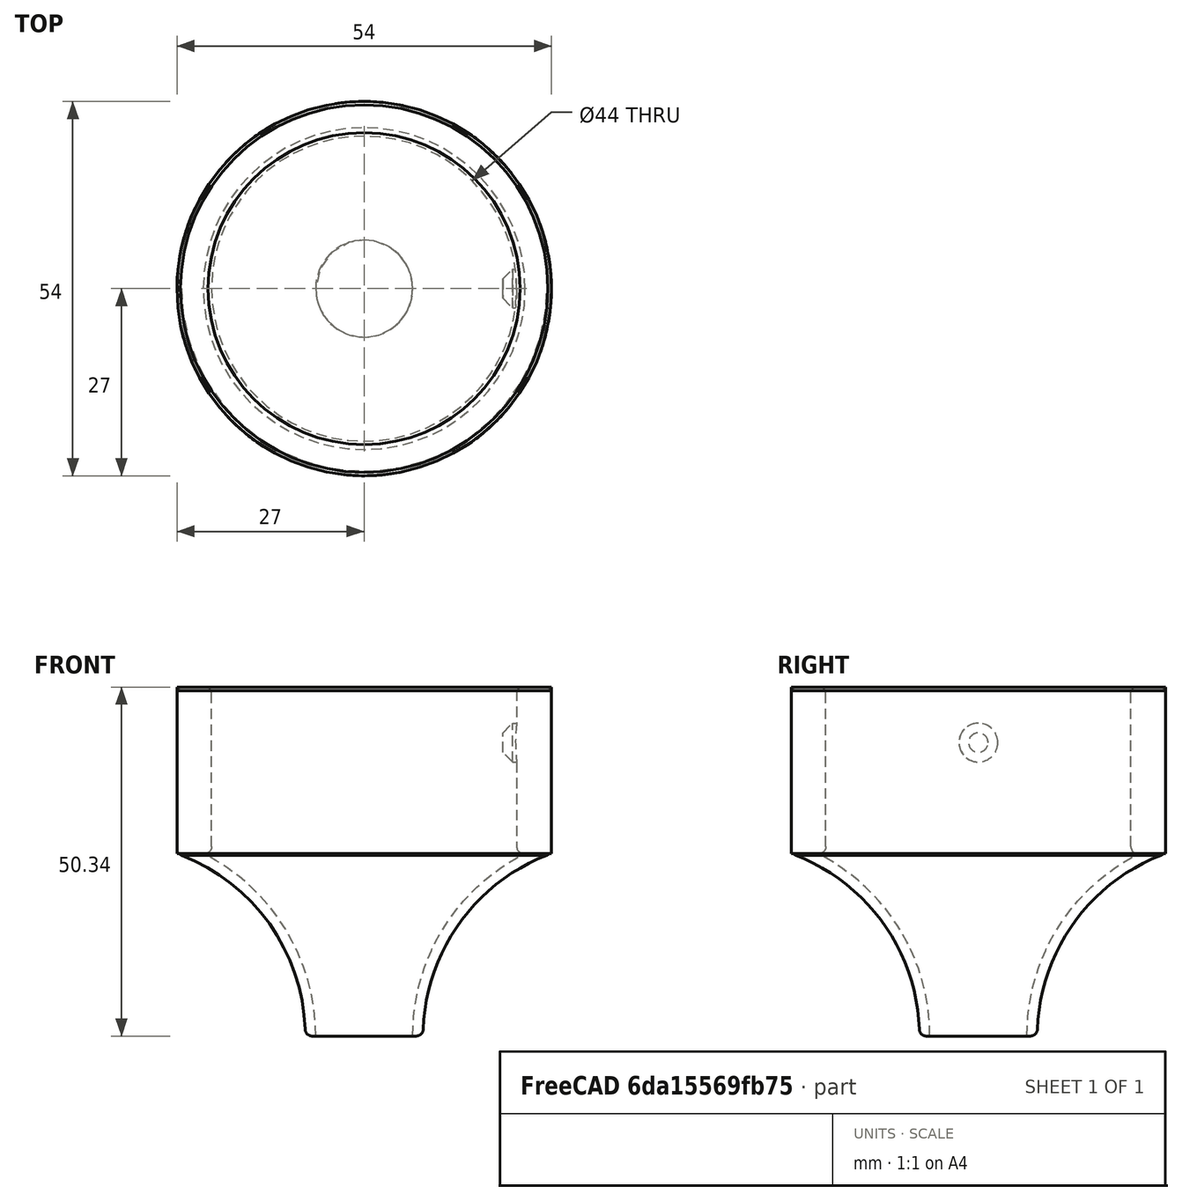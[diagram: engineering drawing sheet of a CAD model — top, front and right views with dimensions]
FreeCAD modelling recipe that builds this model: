
FCSTD DOCUMENT  (FreeCAD 0.16R)
Label: BlowerNozzle
License: All rights reserved
LicenseURL: http://en.wikipedia.org/wiki/All_rights_reserved
objects: Sketcher::SketchObject×3, Part::Fillet×2, Part::Chamfer×2, PartDesign::Pad×1, PartDesign::Pocket×1, PartDesign::Revolution×1, Part::Cylinder×1, Part::MultiFuse×1, Mesh::Feature×1
note: 15 computed .brp shape members not serialized (recipe doc carries the construction recipe); baked Part::Feature solids carry a one-line shape summary decoded from their .brp

FEATURE [Sketcher::SketchObject] Sketch
  sketch-geometry (1):
    g0: Circle CenterX=0 CenterY=0 CenterZ=0 NormalX=0 NormalY=0 NormalZ=1 Radius=27
  constraints (2):
    c: Radius(g0) = 27
    c: Coincident(g0,g-1)
FEATURE [PartDesign::Pad] Pad
  Length = 24
  Length2 = 100
  Sketch = -> Sketch
  Type = 0
FEATURE [Sketcher::SketchObject] Sketch001
  Placement = pos=(0,0,24) rot=(0,0,1;0rad)
  Support = -> Pad [Face3]
  sketch-geometry (1):
    g0: Circle CenterX=0 CenterY=0 CenterZ=0 NormalX=0 NormalY=0 NormalZ=1 Radius=22
  constraints (2):
    c: Coincident(g0,g-1)
    c: Radius(g0) = 22
FEATURE [PartDesign::Pocket] Pocket
  Length = 5
  Sketch = -> Sketch001
  Type = 1
FEATURE [Sketcher::SketchObject] Sketch002
  Placement = pos=(0,0,0) rot=(-1,0,0;4.71239rad)
  sketch-geometry (5):
    g0: ArcOfCircle CenterX=-36.5 CenterY=-26.3391 CenterZ=0 NormalX=0 NormalY=0 NormalZ=1 Radius=28 StartAngle=6.28318 EndAngle=7.50782
    g1: ArcOfCircle CenterX=-36.5 CenterY=-26.3391 CenterZ=0 NormalX=0 NormalY=0 NormalZ=1 Radius=29.5 StartAngle=6.28318 EndAngle=7.38682
    g2: LineSegment [constr] StartX=-7 StartY=-13.456 StartZ=0 EndX=-7 EndY=-26.3392 EndZ=0
    g3: LineSegment StartX=-8.5 StartY=-26.3392 StartZ=0 EndX=-7 EndY=-26.3392 EndZ=0
    g4: LineSegment StartX=-27 StartY=0 StartZ=0 EndX=-23.2147 EndY=0 EndZ=0
  constraints (16):
    c: Radius(g0) = 28
    c: Coincident(g1,g0)
    c: Radius(g1) = 29.5
    c: Vertical(g2)
    c: DistanceX(g2) = -7
    c: Coincident(g1,g2)
    c: Tangent(g1,g2)
    c: PointOnObject(g1,g-1)
    c: DistanceX(g0) = -27
    c: PointOnObject(g0,g-1)
    c: Coincident(g3,g0)
    c: Coincident(g3,g1)
    c: Horizontal(g3)
    c: Coincident(g4,g0)
    c: Coincident(g4,g1)
    c: Distance(g2) = 12.8832
FEATURE [PartDesign::Revolution] Revolution
  Angle = 360
  Axis = (0,0,1)
  Base = (0,0,0)
  Placement = pos=(0,0,0) rot=(-1,0,0;4.71239rad)
  ReferenceAxis = -> Sketch002 [V_Axis]
  Sketch = -> Sketch002
FEATURE [Part::Cylinder] Cylinder
  Angle = 360
  Height = 5
  Placement = pos=(20,0,16) rot=(0,1,0;1.5708rad)
  Radius = 2.8
FEATURE [Part::MultiFuse] Fusion
  Shapes = -> [Pocket,Revolution,Cylinder]
FEATURE [Part::Fillet] Fillet
  Base = -> Fusion
  Edges = 2 edges r=1: [Edge4,Edge9]
FEATURE [Part::Fillet] Fillet001
  Base = -> Fillet
  Edges = 1 edges r=1: [Edge11]
FEATURE [Part::Chamfer] Chamfer
  Base = -> Fillet001
  Edges = 2 edges r=0.5: [Edge13,Edge16]
FEATURE [Part::Chamfer] Chamfer001
  Base = -> Chamfer
  Edges = 1 edges r=1.4: [Edge25]
FEATURE [Mesh::Feature] Mesh  label="Chamfer001 (Meshed)"
